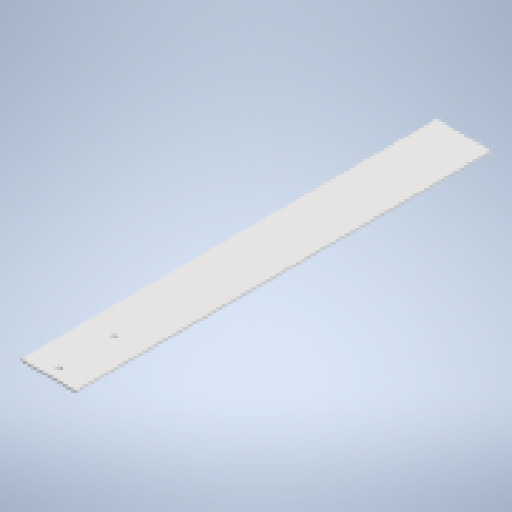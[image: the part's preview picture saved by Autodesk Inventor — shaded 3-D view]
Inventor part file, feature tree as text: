
AUTODESK INVENTOR PART (.ipt)
format: ipt  version: 2023 (Build 270158000, 158)  size: 138,752 bytes
history: native  units: mm
features: extrude x1, sketch x1
ambient origin geometry x8: Origin, YZ Plane, XZ Plane, XY Plane, X Axis, Y Axis, Z Axis, Center Point
bodies: Solid1 (feature_tree)
feature tree (2):
  extrude  "Extrusion1"  Depth=350.0mm
  sketch  "Sketch1"  dims[d0=50.0mm d1=350.0mm d2=10.0mm d3=5.0mm d4=50.0mm d5=5.0mm d6=2.0mm d7=0.0mm]
